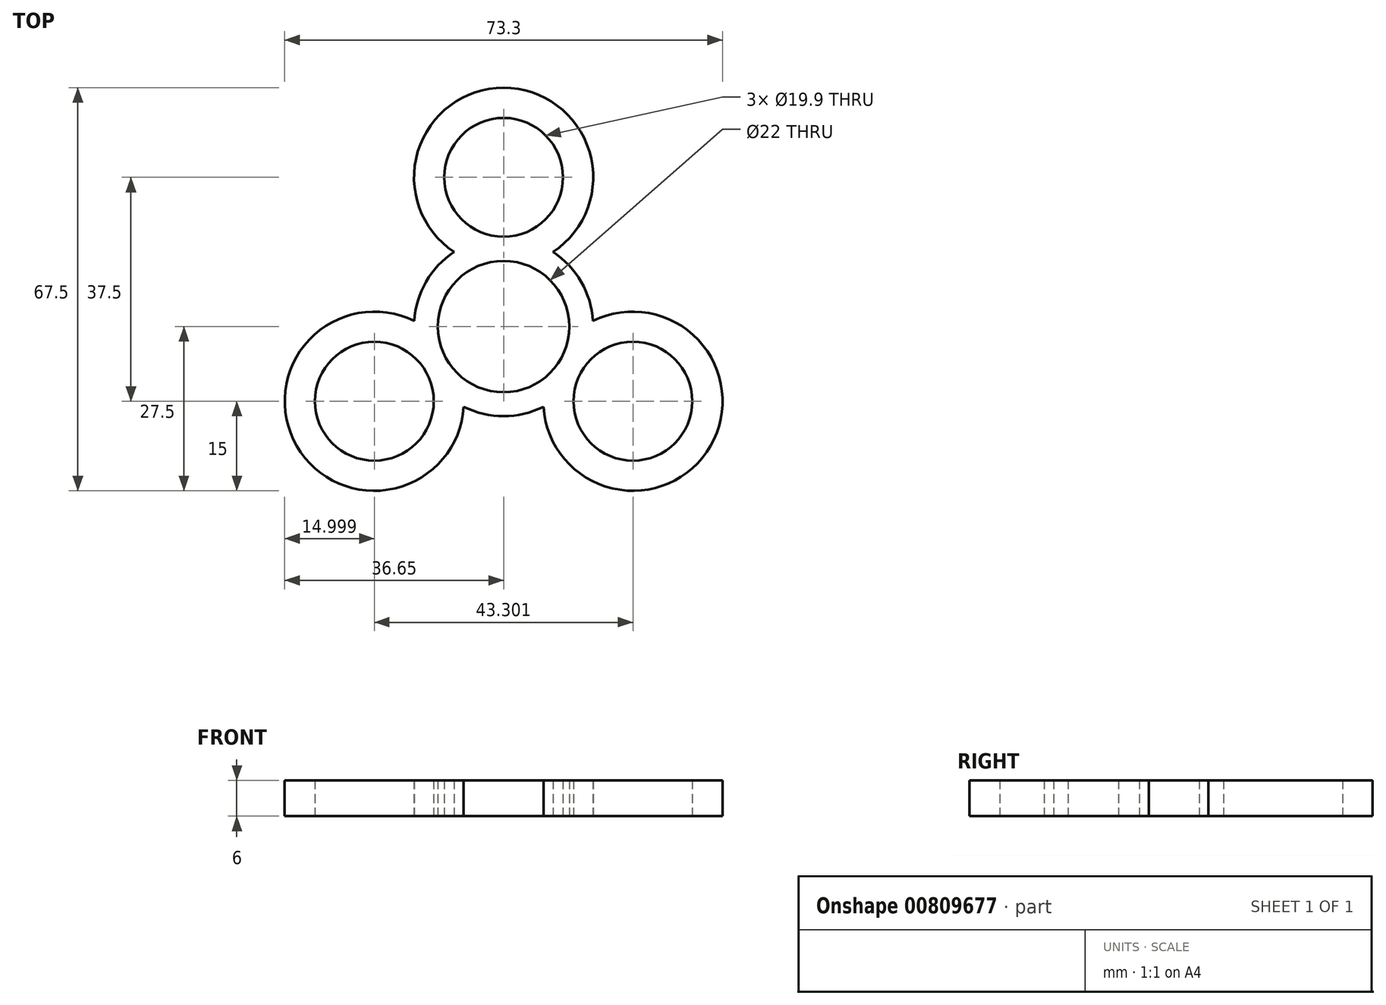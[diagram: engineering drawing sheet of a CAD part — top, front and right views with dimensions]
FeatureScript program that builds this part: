
annotation { "Feature Type Name" : "Feature", "Feature Type Description" : "" }
export const myFeature = defineFeature(function(context is Context, id is Id, definition is map)
    precondition{}
    {
        {
            var Q0;
            Q0=qCreatedBy(makeId("Top.planeOp"),FACE);
            var sketch = newSketch(context, id + "F0", { "sketchPlane" : qUnion([Q0])});
            skArc(sketch, "E0", {"start": v(9.53, 5.5) * mm, "mid": v(0, 11) * mm, "end": v(-9.53, 5.5) * mm});
            skLineSegment(sketch, "E1", {"start": v(0, 0) * mm, "end": v(0, 25) * mm});
            skCircle(sketch, "E2", {"center": v(0, 25) * mm, "radius": 9.95 * mm});
            skArc(sketch, "E3", {"start": v(13, 7.5) * mm, "mid": v(10.93, 10.27) * mm, "end": v(8.3, 12.5) * mm});
            skArc(sketch, "E4", {"start": v(8.3, 12.5) * mm, "mid": v(0, 40) * mm, "end": v(-8.3, 12.5) * mm});
            skArc(sketch, "E5.trimOffspring", {"start": v(-8.3, 12.5) * mm, "mid": v(-10.93, 10.27) * mm, "end": v(-13, 7.5) * mm});
            skArc(sketch, "E6.1.0", {"start": v(-14.97, 0.93) * mm, "mid": v(-34.64, -20) * mm, "end": v(-6.68, -13.43) * mm});
            skArc(sketch, "E6.1.1", {"start": v(-6.68, -13.43) * mm, "mid": v(-3.43, -14.6) * mm, "end": v(0, -15) * mm});
            skArc(sketch, "E6.1.2", {"start": v(-13, 7.5) * mm, "mid": v(-14.36, 4.33) * mm, "end": v(-14.97, 0.93) * mm});
            skCircle(sketch, "E6.1.3", {"center": v(-21.65, -12.5) * mm, "radius": 9.95 * mm});
            skArc(sketch, "E6.1.4", {"start": v(-9.53, 5.5) * mm, "mid": v(-9.53, -5.5) * mm, "end": v(0, -11) * mm});
            skArc(sketch, "E6.2.0", {"start": v(6.68, -13.43) * mm, "mid": v(34.64, -20) * mm, "end": v(14.97, 0.93) * mm});
            skArc(sketch, "E6.2.1", {"start": v(14.97, 0.93) * mm, "mid": v(14.36, 4.33) * mm, "end": v(13, 7.5) * mm});
            skArc(sketch, "E6.2.2", {"start": v(0, -15) * mm, "mid": v(3.43, -14.6) * mm, "end": v(6.68, -13.43) * mm});
            skCircle(sketch, "E6.2.3", {"center": v(21.65, -12.5) * mm, "radius": 9.95 * mm});
            skArc(sketch, "E6.2.4", {"start": v(0, -11) * mm, "mid": v(9.53, -5.5) * mm, "end": v(9.53, 5.5) * mm});
            skSolve(sketch);
        }
        {
            var Q0;
            Q0 = qSketchRegion(id + "F0", true);
            extrude(context, id + "F1", {"entities" : qUnion([Q0]), "depth" : 6 * mm, "offsetDistance" : 25 * mm});
        }
    });
